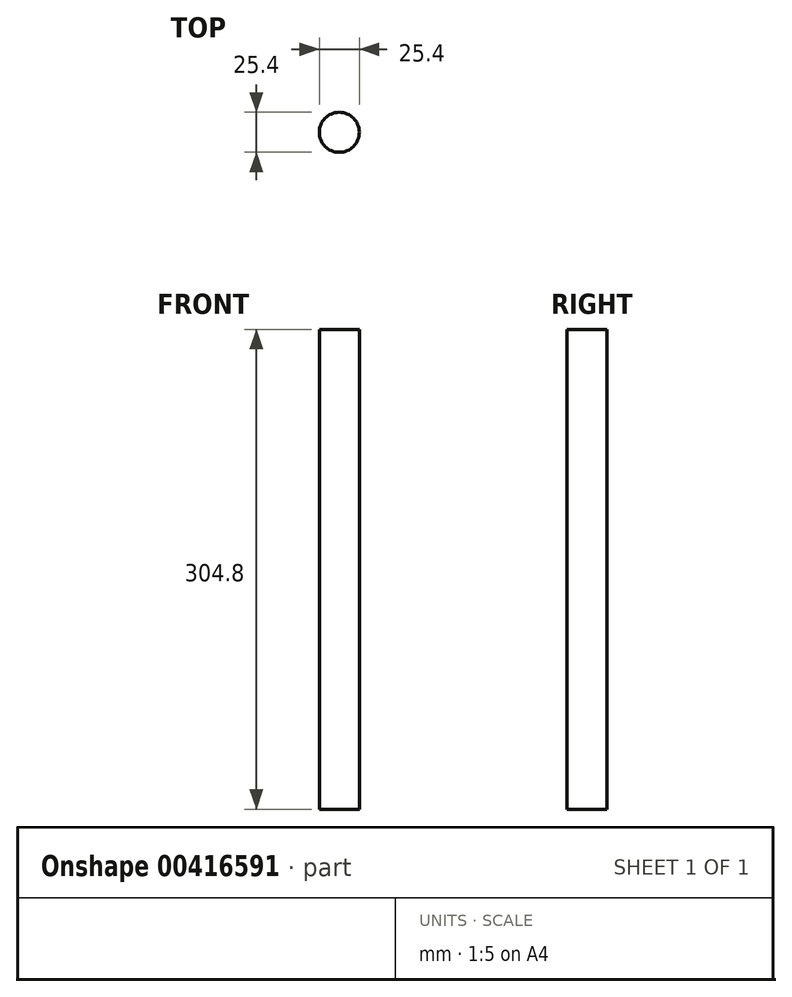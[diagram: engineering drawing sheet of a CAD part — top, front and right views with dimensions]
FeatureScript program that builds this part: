
annotation { "Feature Type Name" : "Feature", "Feature Type Description" : "" }
export const myFeature = defineFeature(function(context is Context, id is Id, definition is map)
    precondition{}
    {
        {
            var Q0;
            Q0=qCreatedBy(makeId("Top.planeOp"),FACE);
            var sketch = newSketch(context, id + "F0", { "sketchPlane" : qUnion([Q0])});
            skCircle(sketch, "E0", {"center": v(0, 0) * mm, "radius": 12.7 * mm});
            skSolve(sketch);
        }
        {
            var Q0;
            Q0 = qSketchRegion(id + "F0", true);
            extrude(context, id + "F1", {"entities" : qUnion([Q0]), "depth" : 304.8 * mm, "offsetDistance" : 25.4 * mm});
        }
        {
            var Q0;
            Q0=makeQuery(id+"F1.opExtrude","SWEPT_BODY",BODY,{"disambiguationData":[OSD([sQuery(id+"F0.wireOp",EDGE,"E0")])]});
            transform(context, id + "F2", {"entities" : qUnion([Q0]), "transformType" : TransformType.TRANSLATION_3D, "dx" : 0 * mm, "dy" : 0 * mm, "dz" : 0 * mm, "makeCopy" : true});
        }
    });
